# Revit family: QF_ZANUSSI_372068_Z7FRGD1BF0
name_source: partatom
category: Specialty Equipment
revit_build: Autodesk Revit 2018 (Build: 20190510_1515(x64)
units: mm (PartAtom-declared; Revit-internal decimal feet)

## family parameters
Always vertical = Yes
Cut with Voids When Loaded = No
Part Type = Normal
Room Calculation Point = No
Round Connector Dimension = Use Diameter
Shared = No
Work Plane-Based = No

## types (1)
- QF_ZANUSSI_372068_Z7FRGD1BF0
    Accessory = Yes
    Cold Water Size = 0"
    Compressed Air Pressure = 0.00 psi
    Compressed Air Size = 0"
    Compressed Air Volume = 0 GPM
    Condensate Return Size = 0"
    Cycle = 0 Hz
    Depth = 715 mm  [stored 2.3458 ft]
    Depth Actual = 700 mm  [stored 2.29659 ft]
    Description = 7 LITRE GAS FRYER 400 MM
    Direct Waste Size = 0"
    Gas Connection Height = 0 mm  [stored 0 ft]
    Gas Size = 1"
    HP = 0 HP
    Height = 333 mm
    Height Actual = 850 mm
    Hot Water Size = 0"
    Length Actual = 400 mm  [stored 1.31234 ft]
    Manufacturer = Zanussi
    Model = Z7FRGD1BF0
    Phase = 0
    Refrigerant Compressor Remote = Yes
    Refrigeration Liquid Line Size = 0"
    Refrigeration Suction Line Size = 0"
    Steam Pounds per Hour = 0
    Steam Supply Maximum Pressure = 0.00 psi
    Steam Supply Minimum Pressure = 0.00 psi
    Steam Supply Size = 0"
    URL = http://www.zanussiprofessional.com
    URL Cutsheet = www.electrolux.com/foodservice
    URL Manufacturer = http://www.zanussiprofessional.com
    Volts = 0 V
    Watts = 0 W
    Weight = 0.00 kg
    Weight in Pounds = 88
    Width = 400 mm  [stored 1.31234 ft]

note: [stored X ft] marks values corroborated as IEEE doubles in the binary element streams (Revit-internal decimal feet)

## geometry (parser evidence)
native form markers: Blend x41, Sweep x2
no freeform markers — native parametric forms only
